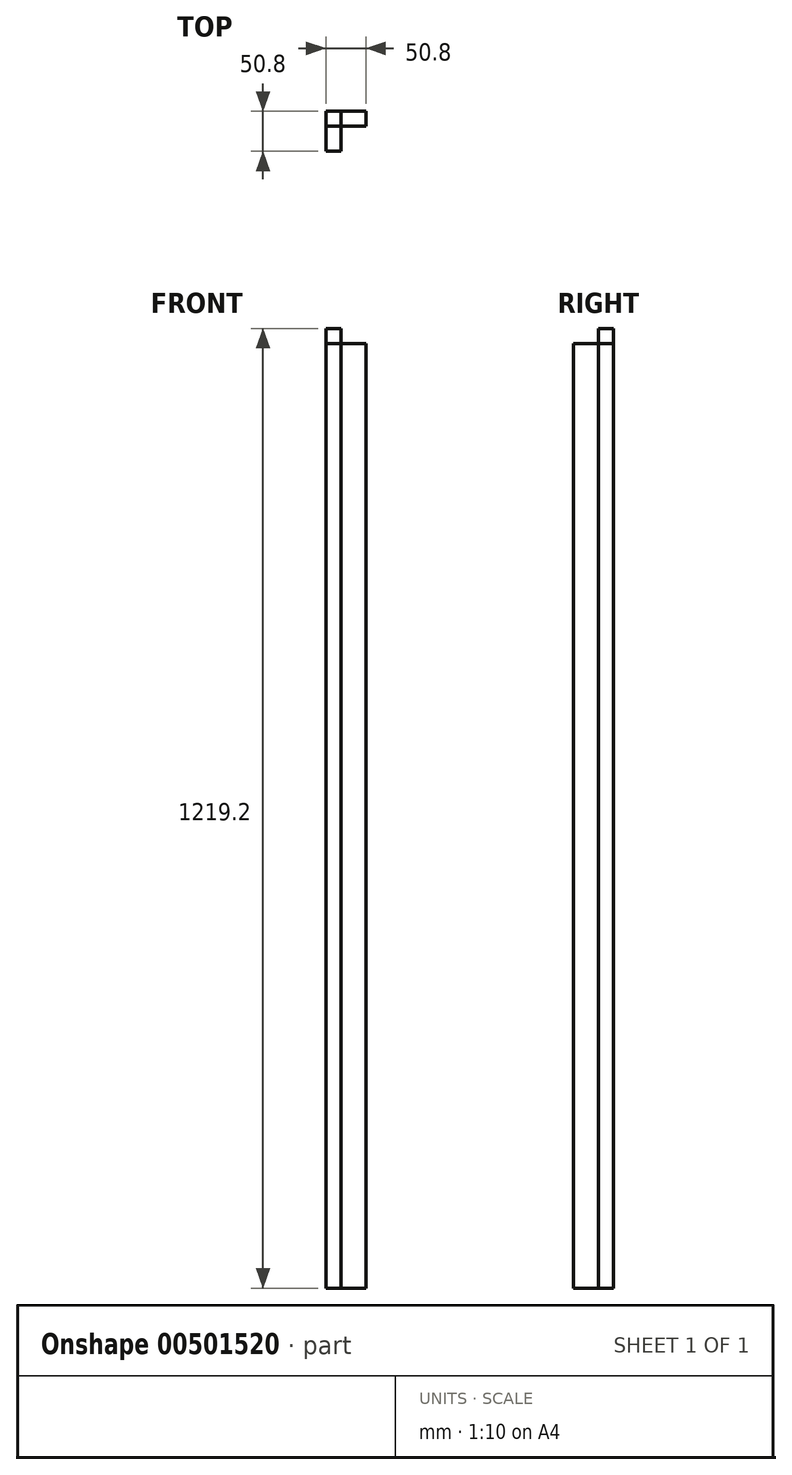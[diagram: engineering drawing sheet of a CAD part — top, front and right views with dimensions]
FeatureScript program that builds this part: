
annotation { "Feature Type Name" : "Feature", "Feature Type Description" : "" }
export const myFeature = defineFeature(function(context is Context, id is Id, definition is map)
    precondition{}
    {
        {
            var Q0;
            Q0=qCreatedBy(makeId("Top.planeOp"),FACE);
            var sketch = newSketch(context, id + "F0", { "sketchPlane" : qUnion([Q0])});
            skLineSegment(sketch, "E0.bottom", {"start": v(0, 0) * mm, "end": v(50.8, 0) * mm});
            skLineSegment(sketch, "E0.top", {"start": v(0, 50.8) * mm, "end": v(50.8, 50.8) * mm});
            skLineSegment(sketch, "E0.left", {"start": v(0, 0) * mm, "end": v(0, 50.8) * mm});
            skLineSegment(sketch, "E0.right", {"start": v(50.8, 0) * mm, "end": v(50.8, 50.8) * mm});
            skSolve(sketch);
        }
        {
            var Q0;
            Q0=makeQuery(id+"F0.imprint","IMPRINT",FACE,{"disambiguationData":[TD([[makeQuery(id+"F0.imprint","IMPRINT",EDGE,{"derivedFrom":sQuery(id+"F0.wireOp",EDGE,"E0.bottom")}),1.0]])]});
            extrude(context, id + "F1", {"entities" : qUnion([Q0]), "oppositeDirection" : true, "depth" : 1219.2 * mm});
        }
        {
            var Q0;
            Q0=makeQuery(id+"F1.opExtrude","CAP_FACE",FACE,{"disambiguationData":[OSD([sQuery(id+"F0.wireOp",EDGE,"E0.bottom"),sQuery(id+"F0.wireOp",EDGE,"E0.top"),sQuery(id+"F0.wireOp",EDGE,"E0.left"),sQuery(id+"F0.wireOp",EDGE,"E0.right")])],"isStart":true});
            var sketch = newSketch(context, id + "F2", { "sketchPlane" : qUnion([Q0])});
            skLineSegment(sketch, "E1", {"start": v(0, 31.75) * mm, "end": v(19.05, 31.75) * mm});
            skLineSegment(sketch, "E2", {"start": v(19.05, 31.75) * mm, "end": v(19.05, 50.8) * mm});
            skLineSegment(sketch, "E3", {"start": v(19.05, 50.8) * mm, "end": v(50.8, 50.8) * mm});
            skLineSegment(sketch, "E4", {"start": v(50.8, 50.8) * mm, "end": v(50.8, 0) * mm});
            skLineSegment(sketch, "E5", {"start": v(50.8, 0) * mm, "end": v(0, 0) * mm});
            skLineSegment(sketch, "E6", {"start": v(0, 0) * mm, "end": v(0, 31.75) * mm});
            skSolve(sketch);
        }
        {
            var Q0;
            Q0=makeQuery(id+"F2.imprint","IMPRINT",FACE,{"disambiguationData":[TD([[makeQuery(id+"F2.imprint","IMPRINT",EDGE,{"derivedFrom":sQuery(id+"F2.wireOp",EDGE,"E1")}),-1.0]])]});
            extrude(context, id + "F3", {"entities" : qUnion([Q0]), "operationType" : NewBodyOperationType.REMOVE, "oppositeDirection" : true, "depth" : 19.05 * mm});
        }
        {
            var Q0;
            Q0=makeQuery(id+"F3.boolean.opBoolean","COPY",FACE,{"derivedFrom":makeQuery(id+"F3.opExtrude","CAP_FACE",FACE,{"disambiguationData":[OSD([sQuery(id+"F2.wireOp",EDGE,"E1"),sQuery(id+"F2.wireOp",EDGE,"E2"),sQuery(id+"F2.wireOp",EDGE,"E3"),sQuery(id+"F2.wireOp",EDGE,"E4"),sQuery(id+"F2.wireOp",EDGE,"E5"),sQuery(id+"F2.wireOp",EDGE,"E6")])],"isStart":false})});
            var sketch = newSketch(context, id + "F4", { "sketchPlane" : qUnion([Q0])});
            skLineSegment(sketch, "E7.bottom", {"start": v(50.8, 0) * mm, "end": v(19.05, 0) * mm});
            skLineSegment(sketch, "E7.top", {"start": v(50.8, 31.75) * mm, "end": v(19.05, 31.75) * mm});
            skLineSegment(sketch, "E7.left", {"start": v(50.8, 0) * mm, "end": v(50.8, 31.75) * mm});
            skLineSegment(sketch, "E7.right", {"start": v(19.05, 0) * mm, "end": v(19.05, 31.75) * mm});
            skSolve(sketch);
        }
        {
            var Q0;
            Q0=makeQuery(id+"F4.imprint","IMPRINT",FACE,{"disambiguationData":[TD([[makeQuery(id+"F4.imprint","IMPRINT",EDGE,{"derivedFrom":sQuery(id+"F4.wireOp",EDGE,"E7.bottom")}),1.0]])]});
            extrude(context, id + "F5", {"entities" : qUnion([Q0]), "operationType" : NewBodyOperationType.REMOVE, "endBound" : BoundingType.THROUGH_ALL, "oppositeDirection" : true, "depth" : 25.4 * mm});
        }
    });
